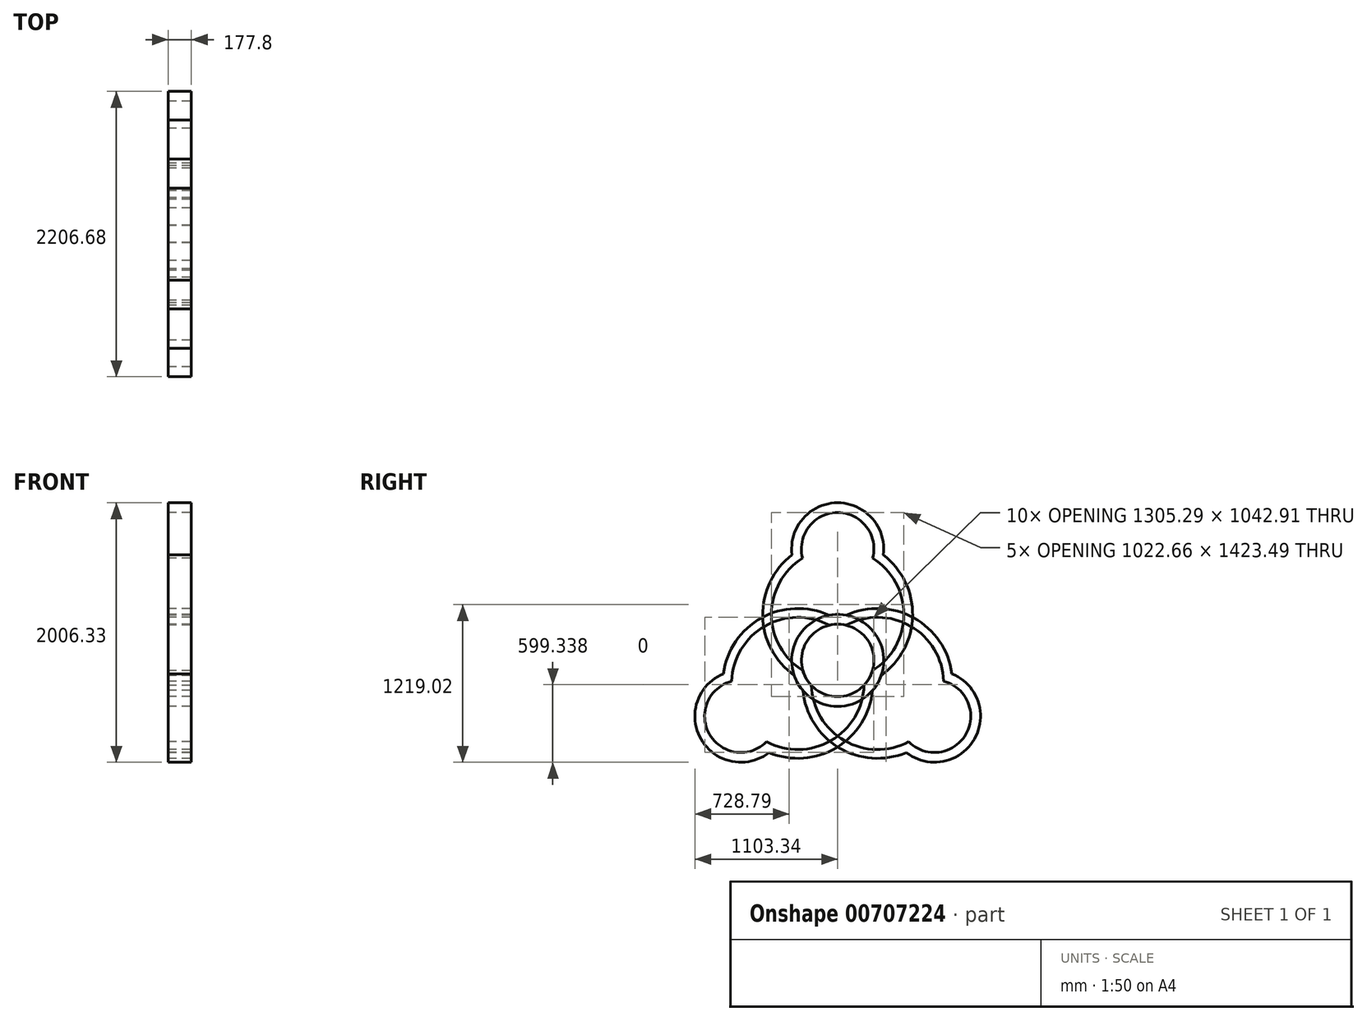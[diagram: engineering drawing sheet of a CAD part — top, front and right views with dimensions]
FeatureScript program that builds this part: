
annotation { "Feature Type Name" : "Feature", "Feature Type Description" : "" }
export const myFeature = defineFeature(function(context is Context, id is Id, definition is map)
    precondition{}
    {
        {
            var Q0;
            Q0=qCreatedBy(makeId("Right.planeOp"),FACE);
            var sketch = newSketch(context, id + "F0", { "sketchPlane" : qUnion([Q0])});
            skCircle(sketch, "E0", {"center": v(0, 0) * mm, "radius": 355.6 * mm});
            skCircle(sketch, "E1", {"center": v(0, 863.42) * mm, "radius": 355.6 * mm});
            skCircle(sketch, "E2", {"center": v(0, 355.6) * mm, "radius": 579.4 * mm});
            skCircle(sketch, "E3", {"center": v(0, 863.42) * mm, "radius": 280.04 * mm});
            skCircle(sketch, "E4", {"center": v(0, 0) * mm, "radius": 280.04 * mm});
            skCircle(sketch, "E5", {"center": v(0, 355.6) * mm, "radius": 511.33 * mm});
            skSolve(sketch);
        }
        {
            var Q0;
            Q0 = qSketchRegion(id + "F0", true);
            var Q1;
            {var subQ0=sQuery(id+"F0.wireOp",EDGE,"E5");var subQ1=sQuery(id+"F0.wireOp",EDGE,"E1");var subQ2=makeQuery(id+"F0.imprint","INTERSECT",VERTEX,{"disambiguationData":[OD(0.0)],"derivedFrom":[subQ1,subQ0]});Q1=makeQuery(id+"F0.imprint","IMPRINT",FACE,{"disambiguationData":[TD([[makeQuery(id+"F0.imprint","IMPRINT",EDGE,{"disambiguationData":[TD([[subQ2,-1.0]])],"derivedFrom":subQ1}),1.0]])]});}
            var Q2;
            {var subQ0=sQuery(id+"F0.wireOp",EDGE,"E5");var subQ1=sQuery(id+"F0.wireOp",EDGE,"E0");var subQ2=makeQuery(id+"F0.imprint","INTERSECT",VERTEX,{"disambiguationData":[OD(0.0)],"derivedFrom":[subQ1,subQ0]});Q2=makeQuery(id+"F0.imprint","IMPRINT",FACE,{"disambiguationData":[TD([[makeQuery(id+"F0.imprint","IMPRINT",EDGE,{"disambiguationData":[TD([[subQ2,1.0]])],"derivedFrom":subQ1}),1.0]])]});}
            extrude(context, id + "F1", {"entities" : qUnion([Q0, Q1, Q2]), "depth" : 177.8 * mm, "offsetDistance" : 25.4 * mm});
        }
        {
            var Q0;
            Q0=makeQuery(id+"F1.opExtrude","SWEPT_BODY",BODY,{"disambiguationData":[OSD([sQuery(id+"F0.wireOp",EDGE,"E0"),sQuery(id+"F0.wireOp",EDGE,"E1"),sQuery(id+"F0.wireOp",EDGE,"E2"),sQuery(id+"F0.wireOp",EDGE,"E3"),sQuery(id+"F0.wireOp",EDGE,"E4"),sQuery(id+"F0.wireOp",EDGE,"E5")])]});
            var Q1;
            {var subQ0=sQuery(id+"F0.wireOp",EDGE,"E2");var subQ1=sQuery(id+"F0.wireOp",EDGE,"E0");Q1=makeQuery(id+"F1.opExtrude","SWEPT_FACE",FACE,{"disambiguationData":[OSD([subQ1]),TDD([makeQuery(id+"F0.imprint","IMPRINT",EDGE,{"disambiguationData":[TD([[makeQuery(id+"F0.imprint","INTERSECT",VERTEX,{"disambiguationData":[OD(0.0)],"derivedFrom":[subQ1,subQ0]}),-1.0]])],"derivedFrom":subQ1})])]});}
            circularPattern(context, id + "F2", {"entities" : qUnion([Q0]), "axis" : qUnion([Q1]), "angle" : 360 * degree, "instanceCount" : 3, "equalSpace" : true});
        }
    });
